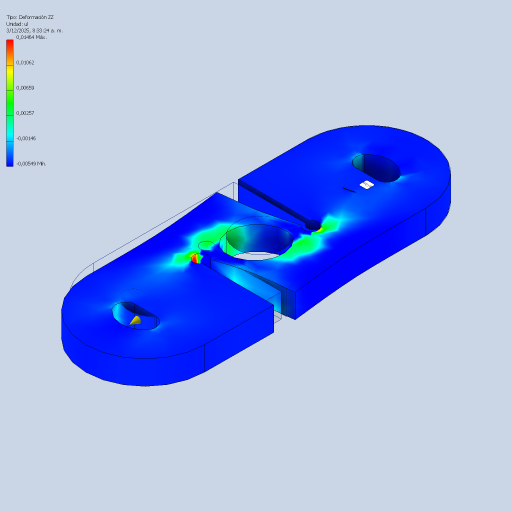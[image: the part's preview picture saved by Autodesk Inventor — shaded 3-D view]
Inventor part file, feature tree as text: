
AUTODESK INVENTOR PART (.ipt)
format: ipt  version: 2024 (Build 280153000, 153)  size: 242,688 bytes
history: native  units: mm
features: extrude x1, fillet x1, sketch x1
ambient origin geometry x8: Origin, YZ Plane, XZ Plane, XY Plane, X Axis, Y Axis, Z Axis, Center Point
bodies: Body1 (feature_tree)
feature tree (3):
  extrude  "Extrusión9"  Depth=50.0mm
  fillet  "Empalme3"  Radius=90.0mm
  sketch  "Boceto1"  dims[d42=50.0mm d43=50.0mm d44=90.0mm d45=20.0mm d46=20.0mm d47=20.0mm d48=5.0mm d49=2.0mm d50=14.0mm d51=5.0mm d52=2.0mm d53=14.0mm d54=10.0mm d55=0.0mm d56=4.0mm d16=1.0mm d17=1.0mm d18=1.0mm d19=0.15mm d20=0.25mm d21=0.375mm d22=14.3117mm d23=0.75mm d24=20.594885mm d25=0.0625mm d26=0.75mm d27=0.375mm]
